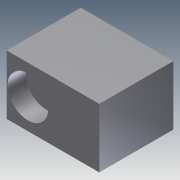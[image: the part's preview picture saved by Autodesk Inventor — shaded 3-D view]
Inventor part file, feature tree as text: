
AUTODESK INVENTOR PART (.ipt)
format: ipt  version: 2011 (Build 150239000, 239)  size: 93,184 bytes
history: native  units: in
note: dims shown in document units (in); Inventor stores cm internally (conversion verified against a paired STEP export)
features: extrude x4, sketch x4
ambient origin geometry x8: Origin, YZ Plane, XZ Plane, XY Plane, X Axis, Y Axis, Z Axis, Center Point
bodies: Solid1 (feature_tree)
feature tree (8):
  extrude  "Extrusion1"  Depth=1.2598in
  extrude  "Extrusion2"  Depth=0.4528in
  extrude  "Extrusion3"  Depth=0.3937in TaperAngle=0.0deg
  extrude  "Extrusion4"  Depth=0.4528in
  sketch  "Sketch1"  dims[d0=1.9685in d1=1.2598in]
  sketch  "Sketch2"  dims[d2=1.5748in d3=0.0in d4=0.4528in]
  sketch  "Sketch3"  dims[d5=0.6299in d6=0.3937in d7=0.0in]
  sketch  "Sketch4"  dims[d8=0.3937in d9=0.0in d10=0.4528in d11=0.8661in d12=0.3937in d13=0.0in]
